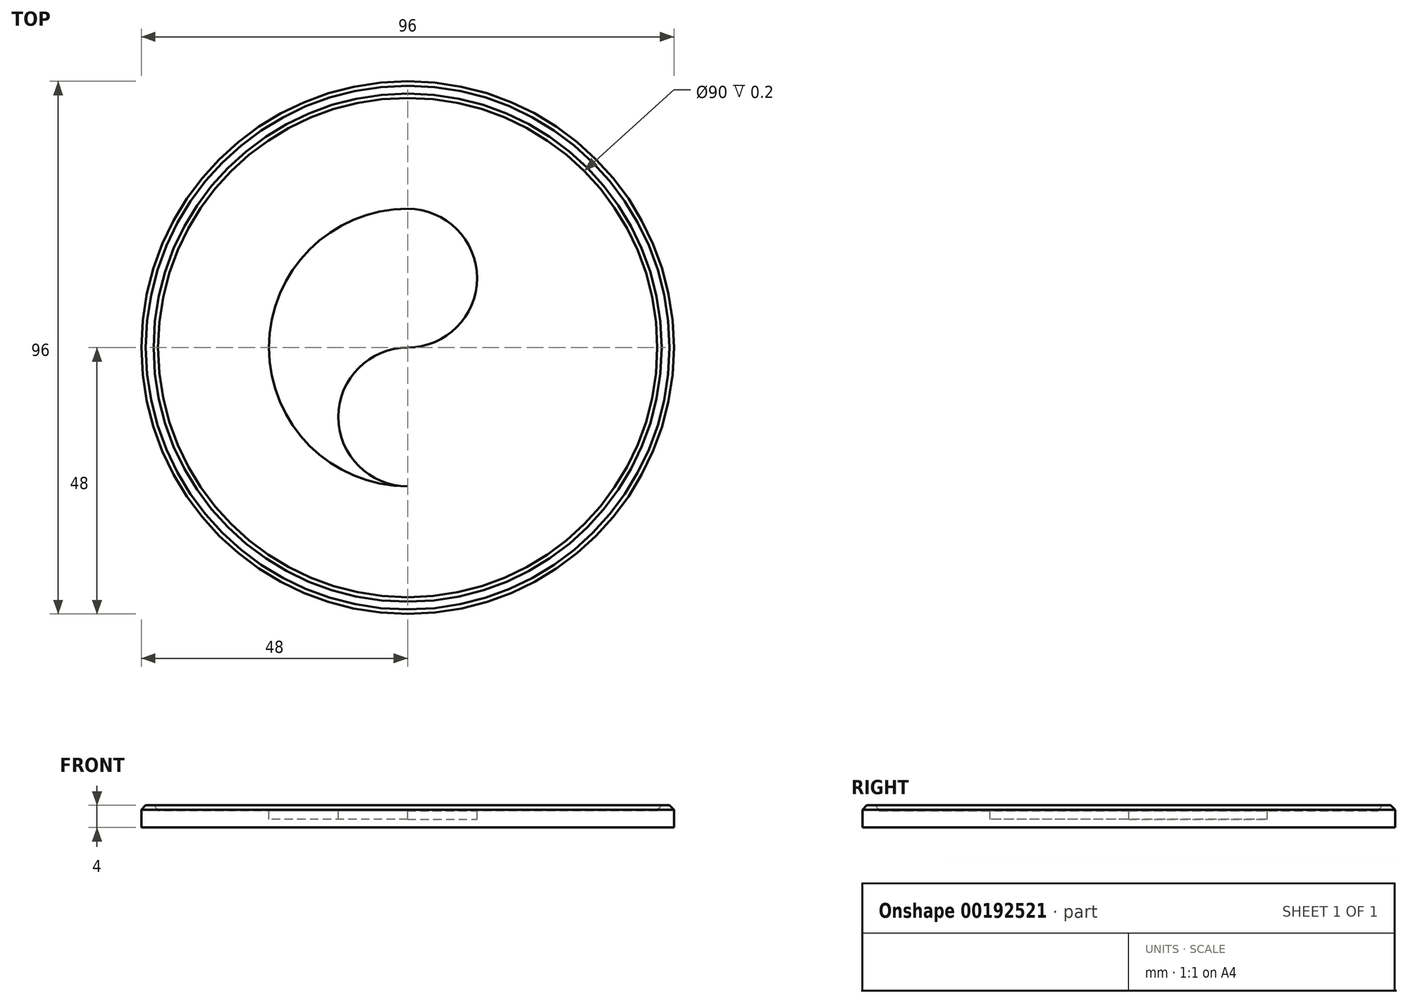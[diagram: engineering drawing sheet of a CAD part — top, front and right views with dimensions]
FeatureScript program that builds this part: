
annotation { "Feature Type Name" : "Feature", "Feature Type Description" : "" }
export const myFeature = defineFeature(function(context is Context, id is Id, definition is map)
    precondition{}
    {
        {
            var Q0;
            Q0=qCreatedBy(makeId("Top.planeOp"),FACE);
            var sketch = newSketch(context, id + "F0", { "sketchPlane" : qUnion([Q0])});
            skCircle(sketch, "E0", {"center": v(0, 0) * mm, "radius": 48 * mm});
            skSolve(sketch);
        }
        {
            var Q0;
            Q0=qSketchRegion(id+"F0",true);
            extrude(context, id + "F1", {"entities" : qUnion([Q0]), "depth" : 3 * mm});
        }
        {
            var Q0;
            Q0=qCreatedBy(makeId("Top.planeOp"),FACE);
            var sketch = newSketch(context, id + "F2", { "sketchPlane" : qUnion([Q0])});
            skCircle(sketch, "E1.0", {"center": v(0, 0) * mm, "radius": 48 * mm});
            skCircle(sketch, "E2.0", {"center": v(0, 0) * mm, "radius": 45 * mm});
            skSolve(sketch);
        }
        {
            var Q0;
            Q0=qSketchRegion(id+"F2",true);
            extrude(context, id + "F3", {"entities" : qUnion([Q0]), "operationType" : NewBodyOperationType.ADD, "depth" : 4 * mm});
        }
        {
            var Q0;
            Q0=makeQuery(id+"F3.opExtrude","CAP_EDGE",EDGE,{"disambiguationData":[OSD([sQuery(id+"F2.wireOp",EDGE,"E1.0")])],"isStart":false});
            var Q1;
            Q1=makeQuery(id+"F3.opExtrude","CAP_EDGE",EDGE,{"disambiguationData":[OSD([sQuery(id+"F2.wireOp",EDGE,"E2.0")])],"isStart":false});
            chamfer(context, id + "F4", {"entities" : qUnion([Q0, Q1]), "width" : 0.8 * mm, "tangentPropagation" : true});
        }
        {
            var Q0;
            Q0=makeQuery(id+"F1.opExtrude","CAP_FACE",FACE,{"disambiguationData":[OSD([sQuery(id+"F0.wireOp",EDGE,"E0")])],"isStart":false});
            var sketch = newSketch(context, id + "F5", { "sketchPlane" : qUnion([Q0])});
            skArc(sketch, "E3", {"start": v(0, 0) * mm, "mid": v(12.5, 12.5) * mm, "end": v(0, 25) * mm});
            skArc(sketch, "E4", {"start": v(0, 25) * mm, "mid": v(-25, 0) * mm, "end": v(0, -25) * mm});
            skArc(sketch, "E5", {"start": v(0, 0) * mm, "mid": v(-12.5, -12.5) * mm, "end": v(0, -25) * mm});
            skSolve(sketch);
        }
        {
            var Q0;
            Q0=qSketchRegion(id+"F5",true);
            extrude(context, id + "F6", {"entities" : qUnion([Q0]), "operationType" : NewBodyOperationType.REMOVE, "oppositeDirection" : true, "depth" : 1.5 * mm});
        }
    });
